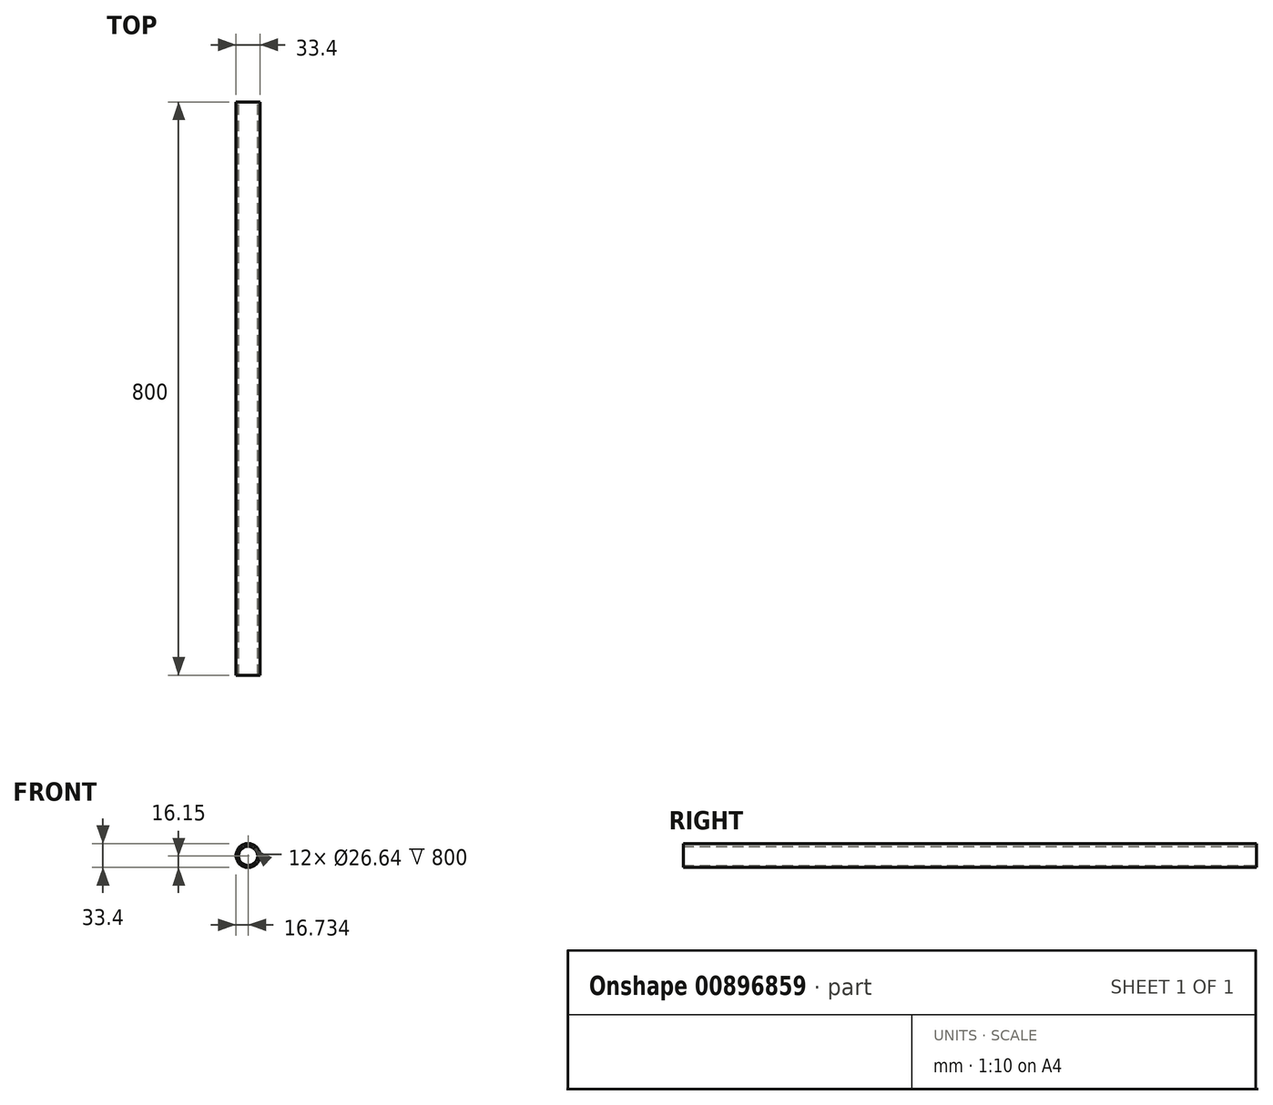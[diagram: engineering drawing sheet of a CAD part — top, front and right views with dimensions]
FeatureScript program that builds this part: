
annotation { "Feature Type Name" : "Feature", "Feature Type Description" : "" }
export const myFeature = defineFeature(function(context is Context, id is Id, definition is map)
    precondition{}
    {
        {
            var Q0;
            Q0=qCreatedBy(makeId("Front.planeOp"),FACE);
            var sketch = newSketch(context, id + "F0", { "sketchPlane" : qUnion([Q0])});
            skCircle(sketch, "E0", {"center": v(0, 0) * mm, "radius": 16.7 * mm});
            skCircle(sketch, "E1", {"center": v(0.03, -0.55) * mm, "radius": 13.32 * mm});
            skSolve(sketch);
        }
        {
            var Q0;
            Q0=makeQuery(id+"F0.imprint","IMPRINT",FACE,{"disambiguationData":[TD([[makeQuery(id+"F0.imprint","IMPRINT",EDGE,{"derivedFrom":sQuery(id+"F0.wireOp",EDGE,"E0")}),1.0]])]});
            extrude(context, id + "F1", {"entities" : qUnion([Q0]), "endBound" : BoundingType.SYMMETRIC, "depth" : 800 * mm, "offsetDistance" : 25.4 * mm});
        }
    });
